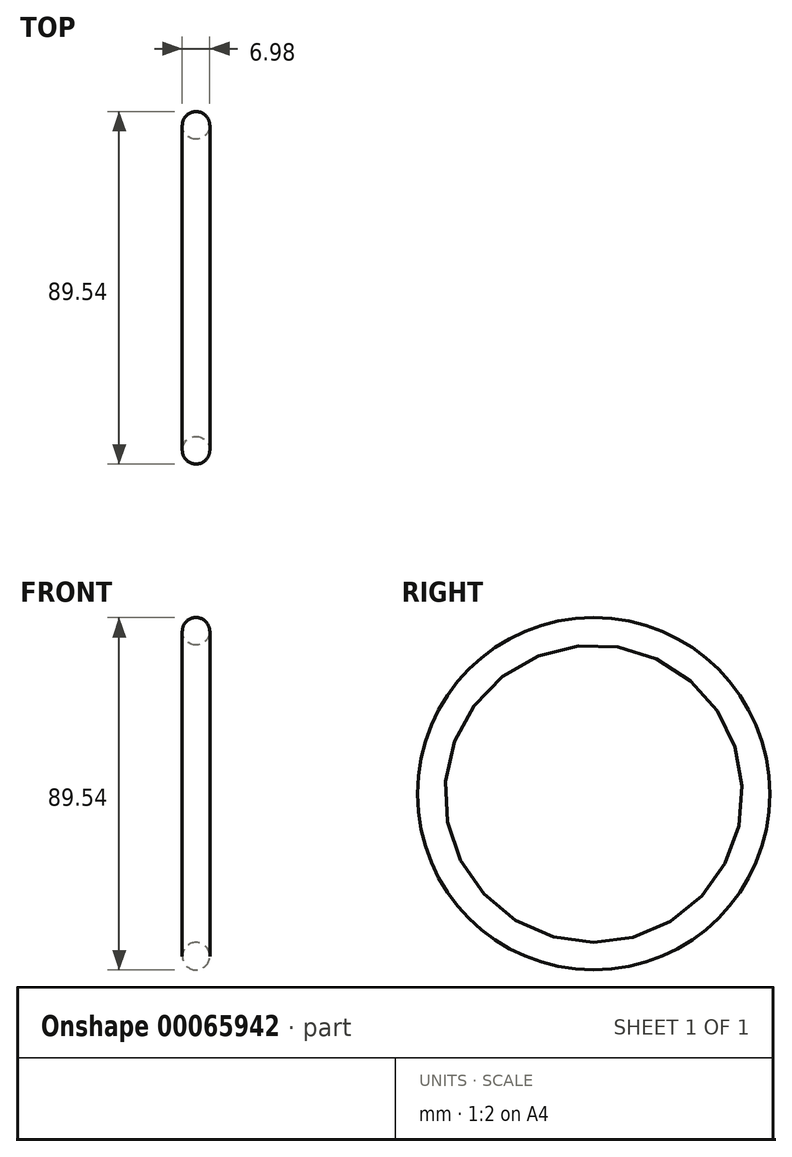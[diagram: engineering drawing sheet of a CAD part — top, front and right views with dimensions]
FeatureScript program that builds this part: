
annotation { "Feature Type Name" : "Feature", "Feature Type Description" : "" }
export const myFeature = defineFeature(function(context is Context, id is Id, definition is map)
    precondition{}
    {
        {
            var Q0;
            Q0=qCreatedBy(makeId("Front.planeOp"),FACE);
            var sketch = newSketch(context, id + "F0", { "sketchPlane" : qUnion([Q0])});
            skLineSegment(sketch, "E0", {"start": v(0, 0) * mm, "end": v(-6.06, 0) * mm, "construction": true});
            skCircle(sketch, "E1", {"center": v(0, 41.28) * mm, "radius": 3.5 * mm});
            skSolve(sketch);
        }
        {
            var Q0;
            Q0=makeQuery(id+"F0.imprint","IMPRINT",FACE,{"disambiguationData":[TD([[makeQuery(id+"F0.imprint","IMPRINT",EDGE,{"derivedFrom":sQuery(id+"F0.wireOp",EDGE,"E1")}),1.0]])]});
            var Q1;
            Q1=sQuery(id+"F0.wireOp",EDGE,"E0");
            revolve(context, id + "F1", {"entities" : qUnion([Q0]), "axis" : qUnion([Q1]), "revolveType" : RevolveType.FULL});
        }
    });
